# Revit family: 511_CA_HL_nailfin
name_source: partatom
category: Windows
units: mm (PartAtom-declared; Revit-internal decimal feet)

## family parameters
Always vertical = Yes
Cut with Voids When Loaded = No
Host = Wall
OmniClass Number = 23.30.20.00
OmniClass Title = Windows
Room Calculation Point = No
Shared = No

## types (21) — shared parameters
Default Sill Height = 31 1/2"
MLW = 3 1/4"
Wall Closure = By host

## per-type parameters (varying)
| type | Height | MLH | Setback | Width |
| 42x72Max | 72" | 36" | 1 11/16" | 42" |
| 30x72 | 72" | 36" | 2" | 30" |
| 15.75x21Min | 21" | 10 1/2" | 2" | 15 3/4" |
| 24x60 | 60" | 30" | 2" | 24" |
| 24x24 | 24" | 12" | 2" | 24" |
| 24x30 | 30" | 15" | 2" | 24" |
| 24x36 | 36" | 18" | 2" | 24" |
| 24x42 | 42" | 21" | 2" | 24" |
| 24x48 | 48" | 24" | 2" | 24" |
| 24x54 | 54" | 27" | 2" | 24" |
| 30x30 | 30" | 15" | 2" | 30" |
| 30x36 | 36" | 18" | 2" | 30" |
| 30x42 | 42" | 21" | 2" | 30" |
| 30x48 | 48" | 24" | 2" | 30" |
| 30x54 | 54" | 27" | 2" | 30" |
| 30x60 | 60" | 30" | 2" | 30" |
| 30x66 | 66" | 33" | 2" | 30" |
| 36x36 | 36" | 18" | 2" | 36" |
| 36x42 | 42" | 21" | 2" | 36" |
| 36x48 | 48" | 24" | 2" | 36" |
| 36x54 | 54" | 27" | 2" | 36" |

## geometry (parser evidence)
native form markers: Sweep x1
no freeform markers — native parametric forms only
